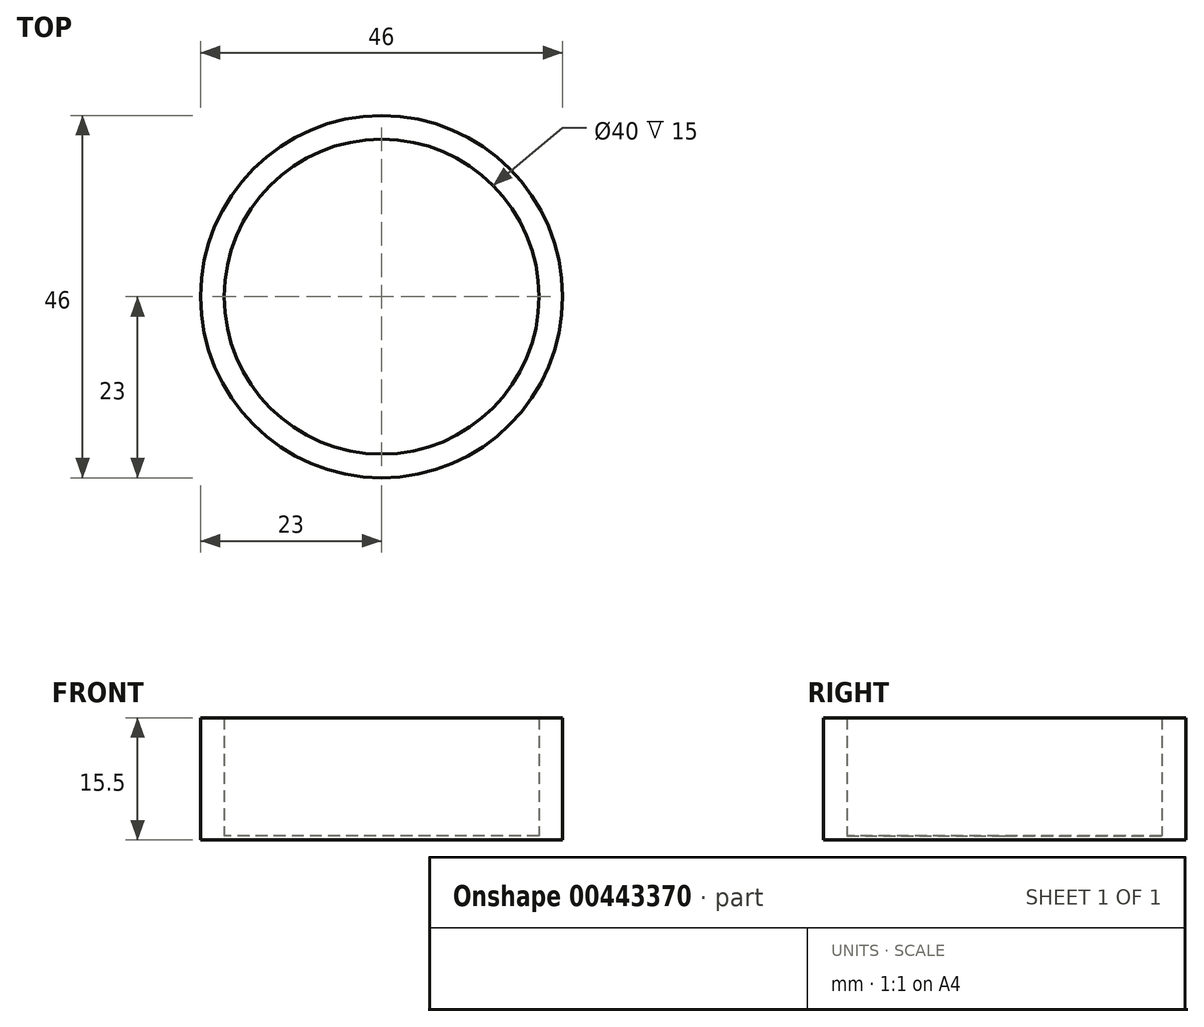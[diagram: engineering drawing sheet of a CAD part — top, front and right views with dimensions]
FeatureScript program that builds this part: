
annotation { "Feature Type Name" : "Feature", "Feature Type Description" : "" }
export const myFeature = defineFeature(function(context is Context, id is Id, definition is map)
    precondition{}
    {
        {
            var Q0;
            Q0=qCreatedBy(makeId("Top.planeOp"),FACE);
            var sketch = newSketch(context, id + "F0", { "sketchPlane" : qUnion([Q0])});
            skCircle(sketch, "E0", {"center": v(0, 0) * mm, "radius": 23 * mm});
            skCircle(sketch, "E1", {"center": v(0, 0) * mm, "radius": 20 * mm});
            skSolve(sketch);
        }
        {
            var Q0;
            Q0=makeQuery(id+"F0.imprint","IMPRINT",FACE,{"disambiguationData":[TD([[makeQuery(id+"F0.imprint","IMPRINT",EDGE,{"derivedFrom":sQuery(id+"F0.wireOp",EDGE,"E0")}),1.0]])]});
            extrude(context, id + "F1", {"entities" : qUnion([Q0]), "depth" : 15 * mm});
        }
        {
            var Q0;
            Q0=qCreatedBy(makeId("Top.planeOp"),FACE);
            var sketch = newSketch(context, id + "F2", { "sketchPlane" : qUnion([Q0])});
            skCircle(sketch, "E2", {"center": v(0, 0) * mm, "radius": 23 * mm});
            skSolve(sketch);
        }
        {
            var Q0;
            Q0 = qSketchRegion(id + "F2", true);
            extrude(context, id + "F3", {"entities" : qUnion([Q0]), "operationType" : NewBodyOperationType.ADD, "oppositeDirection" : true, "depth" : 0.5 * mm});
        }
    });
